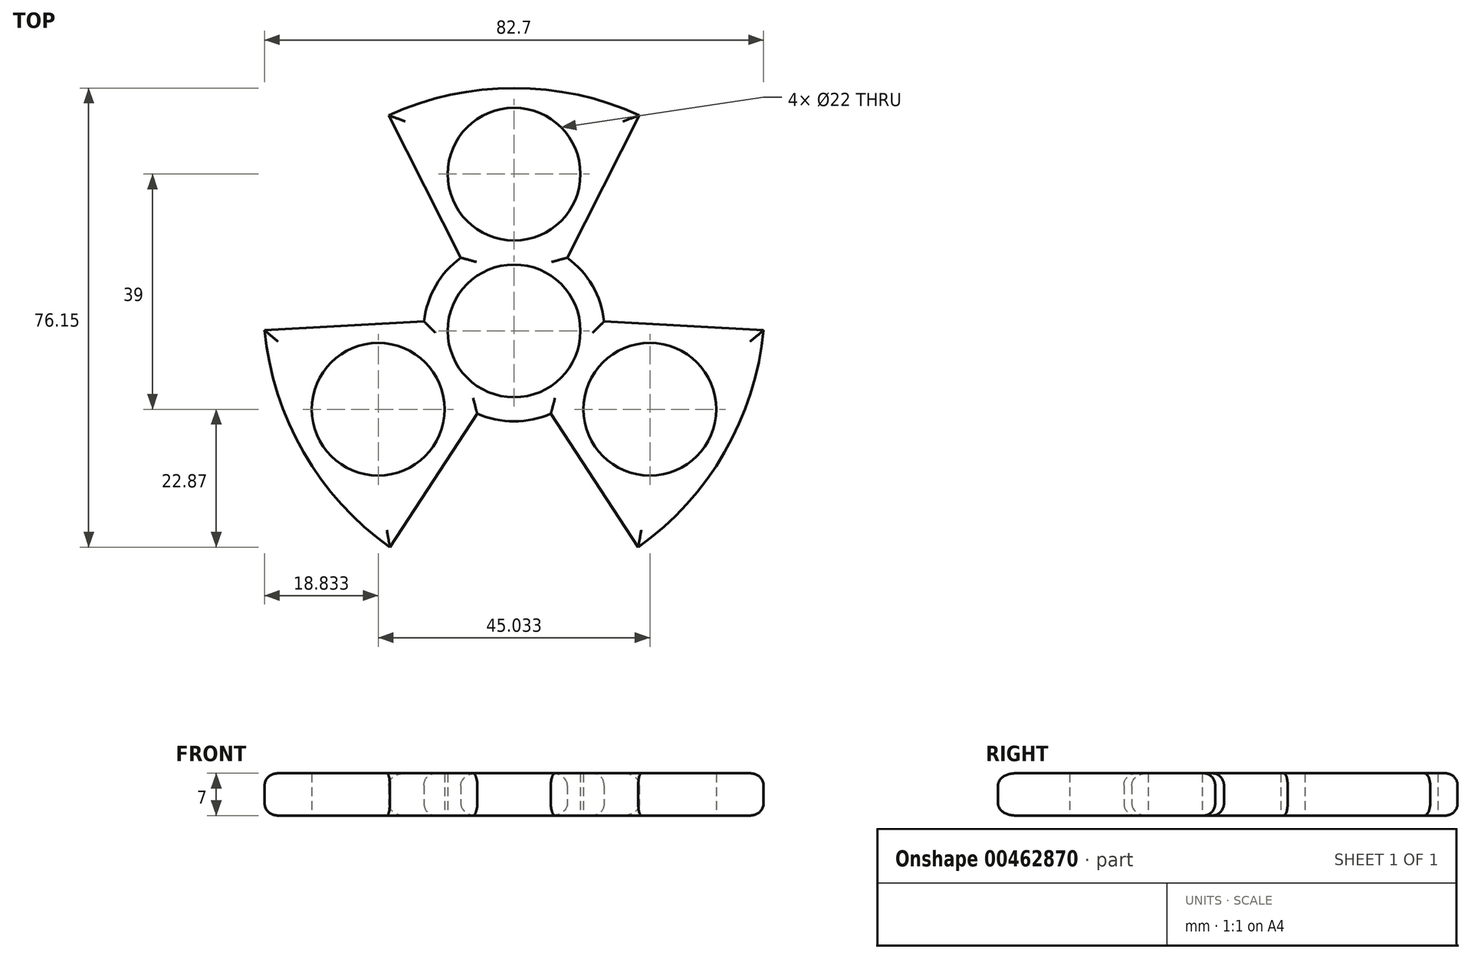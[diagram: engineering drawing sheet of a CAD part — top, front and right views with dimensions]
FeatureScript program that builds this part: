
annotation { "Feature Type Name" : "Feature", "Feature Type Description" : "" }
export const myFeature = defineFeature(function(context is Context, id is Id, definition is map)
    precondition{}
    {
        {
            var Q0;
            Q0=qCreatedBy(makeId("Top.planeOp"),FACE);
            var sketch = newSketch(context, id + "F0", { "sketchPlane" : qUnion([Q0])});
            skCircle(sketch, "E0", {"center": v(0, 0) * mm, "radius": 11 * mm});
            skArc(sketch, "E1", {"start": v(-6.1, -13.7) * mm, "mid": v(0, -15) * mm, "end": v(6.1, -13.7) * mm});
            skCircle(sketch, "E2", {"center": v(0, 26) * mm, "radius": 11 * mm});
            skLineSegment(sketch, "E3", {"start": v(-8.82, 12.13) * mm, "end": v(-20.78, 35.75) * mm});
            skLineSegment(sketch, "E4.MirrorCS", {"start": v(8.82, 12.13) * mm, "end": v(20.78, 35.75) * mm});
            skArc(sketch, "E5", {"start": v(20.78, 35.75) * mm, "mid": v(0, 40.28) * mm, "end": v(-20.78, 35.75) * mm});
            skLineSegment(sketch, "E6.1.0", {"start": v(-6.1, -13.7) * mm, "end": v(-20.57, -35.87) * mm});
            skArc(sketch, "E6.1.1", {"start": v(-41.35, 0.12) * mm, "mid": v(-34.89, -20.14) * mm, "end": v(-20.57, -35.87) * mm});
            skCircle(sketch, "E6.1.2", {"center": v(-22.52, -13) * mm, "radius": 11 * mm});
            skLineSegment(sketch, "E6.1.3", {"start": v(-14.92, 1.57) * mm, "end": v(-41.35, 0.12) * mm});
            skLineSegment(sketch, "E6.2.0", {"start": v(14.92, 1.57) * mm, "end": v(41.35, 0.12) * mm});
            skArc(sketch, "E6.2.1", {"start": v(20.57, -35.87) * mm, "mid": v(34.89, -20.14) * mm, "end": v(41.35, 0.12) * mm});
            skCircle(sketch, "E6.2.2", {"center": v(22.52, -13) * mm, "radius": 11 * mm});
            skLineSegment(sketch, "E6.2.3", {"start": v(6.1, -13.7) * mm, "end": v(20.57, -35.87) * mm});
            skArc(sketch, "E7.trimOffspring", {"start": v(-8.82, 12.13) * mm, "mid": v(-13, 7.5) * mm, "end": v(-14.92, 1.57) * mm});
            skArc(sketch, "E8.trimOffspring", {"start": v(14.92, 1.57) * mm, "mid": v(13, 7.5) * mm, "end": v(8.82, 12.13) * mm});
            skSolve(sketch);
        }
        {
            var Q0;
            Q0=makeQuery(id+"F0.imprint","IMPRINT",FACE,{"disambiguationData":[TD([[makeQuery(id+"F0.imprint","IMPRINT",EDGE,{"derivedFrom":sQuery(id+"F0.wireOp",EDGE,"E0")}),-1.0]])]});
            extrude(context, id + "F1", {"entities" : qUnion([Q0]), "depth" : 7 * mm});
        }
        {
            var Q0;
            Q0=makeQuery(id+"F1.opExtrude","CAP_EDGE",EDGE,{"disambiguationData":[OSD([sQuery(id+"F0.wireOp",EDGE,"E7.trimOffspring")])],"isStart":false});
            var Q1;
            Q1=makeQuery(id+"F1.opExtrude","CAP_EDGE",EDGE,{"disambiguationData":[OSD([sQuery(id+"F0.wireOp",EDGE,"E3")])],"isStart":false});
            var Q2;
            Q2=makeQuery(id+"F1.opExtrude","CAP_EDGE",EDGE,{"disambiguationData":[OSD([sQuery(id+"F0.wireOp",EDGE,"E5")])],"isStart":false});
            var Q3;
            Q3=makeQuery(id+"F1.opExtrude","CAP_EDGE",EDGE,{"disambiguationData":[OSD([sQuery(id+"F0.wireOp",EDGE,"E4.MirrorCS")])],"isStart":false});
            var Q4;
            Q4=makeQuery(id+"F1.opExtrude","CAP_EDGE",EDGE,{"disambiguationData":[OSD([sQuery(id+"F0.wireOp",EDGE,"E8.trimOffspring")])],"isStart":false});
            var Q5;
            Q5=makeQuery(id+"F1.opExtrude","CAP_EDGE",EDGE,{"disambiguationData":[OSD([sQuery(id+"F0.wireOp",EDGE,"E6.2.0")])],"isStart":false});
            var Q6;
            Q6=makeQuery(id+"F1.opExtrude","CAP_EDGE",EDGE,{"disambiguationData":[OSD([sQuery(id+"F0.wireOp",EDGE,"E6.2.1")])],"isStart":false});
            var Q7;
            Q7=makeQuery(id+"F1.opExtrude","CAP_EDGE",EDGE,{"disambiguationData":[OSD([sQuery(id+"F0.wireOp",EDGE,"E6.2.3")])],"isStart":false});
            var Q8;
            Q8=makeQuery(id+"F1.opExtrude","CAP_EDGE",EDGE,{"disambiguationData":[OSD([sQuery(id+"F0.wireOp",EDGE,"E1")])],"isStart":false});
            var Q9;
            Q9=makeQuery(id+"F1.opExtrude","CAP_EDGE",EDGE,{"disambiguationData":[OSD([sQuery(id+"F0.wireOp",EDGE,"E6.1.0")])],"isStart":false});
            var Q10;
            Q10=makeQuery(id+"F1.opExtrude","CAP_EDGE",EDGE,{"disambiguationData":[OSD([sQuery(id+"F0.wireOp",EDGE,"E6.1.1")])],"isStart":false});
            var Q11;
            Q11=makeQuery(id+"F1.opExtrude","CAP_EDGE",EDGE,{"disambiguationData":[OSD([sQuery(id+"F0.wireOp",EDGE,"E6.1.3")])],"isStart":false});
            var Q12;
            Q12=makeQuery(id+"F1.opExtrude","CAP_EDGE",EDGE,{"disambiguationData":[OSD([sQuery(id+"F0.wireOp",EDGE,"E5")])],"isStart":true});
            var Q13;
            Q13=makeQuery(id+"F1.opExtrude","CAP_EDGE",EDGE,{"disambiguationData":[OSD([sQuery(id+"F0.wireOp",EDGE,"E3")])],"isStart":true});
            var Q14;
            Q14=makeQuery(id+"F1.opExtrude","CAP_EDGE",EDGE,{"disambiguationData":[OSD([sQuery(id+"F0.wireOp",EDGE,"E4.MirrorCS")])],"isStart":true});
            var Q15;
            Q15=makeQuery(id+"F1.opExtrude","CAP_EDGE",EDGE,{"disambiguationData":[OSD([sQuery(id+"F0.wireOp",EDGE,"E8.trimOffspring")])],"isStart":true});
            var Q16;
            Q16=makeQuery(id+"F1.opExtrude","CAP_EDGE",EDGE,{"disambiguationData":[OSD([sQuery(id+"F0.wireOp",EDGE,"E6.2.0")])],"isStart":true});
            var Q17;
            Q17=makeQuery(id+"F1.opExtrude","CAP_EDGE",EDGE,{"disambiguationData":[OSD([sQuery(id+"F0.wireOp",EDGE,"E6.2.3")])],"isStart":true});
            var Q18;
            Q18=makeQuery(id+"F1.opExtrude","CAP_EDGE",EDGE,{"disambiguationData":[OSD([sQuery(id+"F0.wireOp",EDGE,"E6.2.1")])],"isStart":true});
            var Q19;
            Q19=makeQuery(id+"F1.opExtrude","CAP_EDGE",EDGE,{"disambiguationData":[OSD([sQuery(id+"F0.wireOp",EDGE,"E6.1.0")])],"isStart":true});
            var Q20;
            Q20=makeQuery(id+"F1.opExtrude","CAP_EDGE",EDGE,{"disambiguationData":[OSD([sQuery(id+"F0.wireOp",EDGE,"E1")])],"isStart":true});
            var Q21;
            Q21=makeQuery(id+"F1.opExtrude","CAP_EDGE",EDGE,{"disambiguationData":[OSD([sQuery(id+"F0.wireOp",EDGE,"E6.1.1")])],"isStart":true});
            var Q22;
            Q22=makeQuery(id+"F1.opExtrude","CAP_EDGE",EDGE,{"disambiguationData":[OSD([sQuery(id+"F0.wireOp",EDGE,"E6.1.3")])],"isStart":true});
            var Q23;
            Q23=makeQuery(id+"F1.opExtrude","CAP_EDGE",EDGE,{"disambiguationData":[OSD([sQuery(id+"F0.wireOp",EDGE,"E7.trimOffspring")])],"isStart":true});
            fillet(context, id + "F2", {"entities" : qUnion([Q0, Q1, Q2, Q3, Q4, Q5, Q6, Q7, Q8, Q9, Q10, Q11, Q12, Q13, Q14, Q15, Q16, Q17, Q18, Q19, Q20, Q21, Q22, Q23]), "radius" : 2 * mm, "tangentPropagation" : true, "allowEdgeOverflow" : false});
        }
    });
